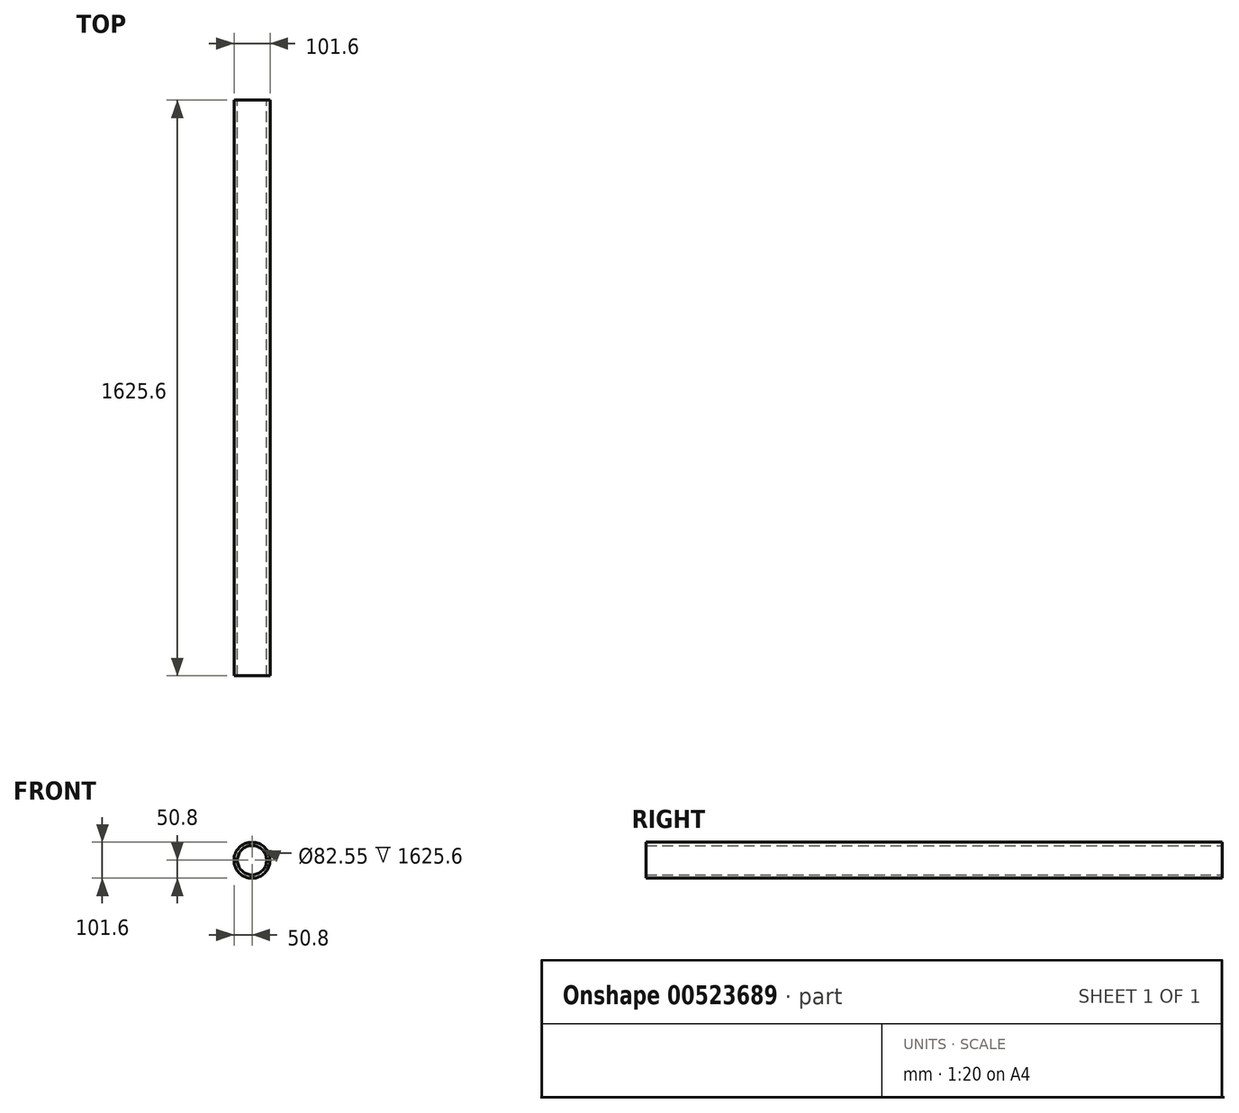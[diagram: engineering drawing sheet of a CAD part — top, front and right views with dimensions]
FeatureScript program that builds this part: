
annotation { "Feature Type Name" : "Feature", "Feature Type Description" : "" }
export const myFeature = defineFeature(function(context is Context, id is Id, definition is map)
    precondition{}
    {
        {
            var Q0;
            Q0=qCreatedBy(makeId("Front.planeOp"),FACE);
            var sketch = newSketch(context, id + "F0", { "sketchPlane" : qUnion([Q0])});
            skCircle(sketch, "E0", {"center": v(0, 0) * mm, "radius": 50.8 * mm});
            skCircle(sketch, "E1", {"center": v(0, 0) * mm, "radius": 41.28 * mm});
            skSolve(sketch);
        }
        {
            var Q0;
            Q0 = qSketchRegion(id + "F0", true);
            extrude(context, id + "F1", {"entities" : qUnion([Q0]), "depth" : 1625.6 * mm, "offsetDistance" : 25.4 * mm});
        }
    });
